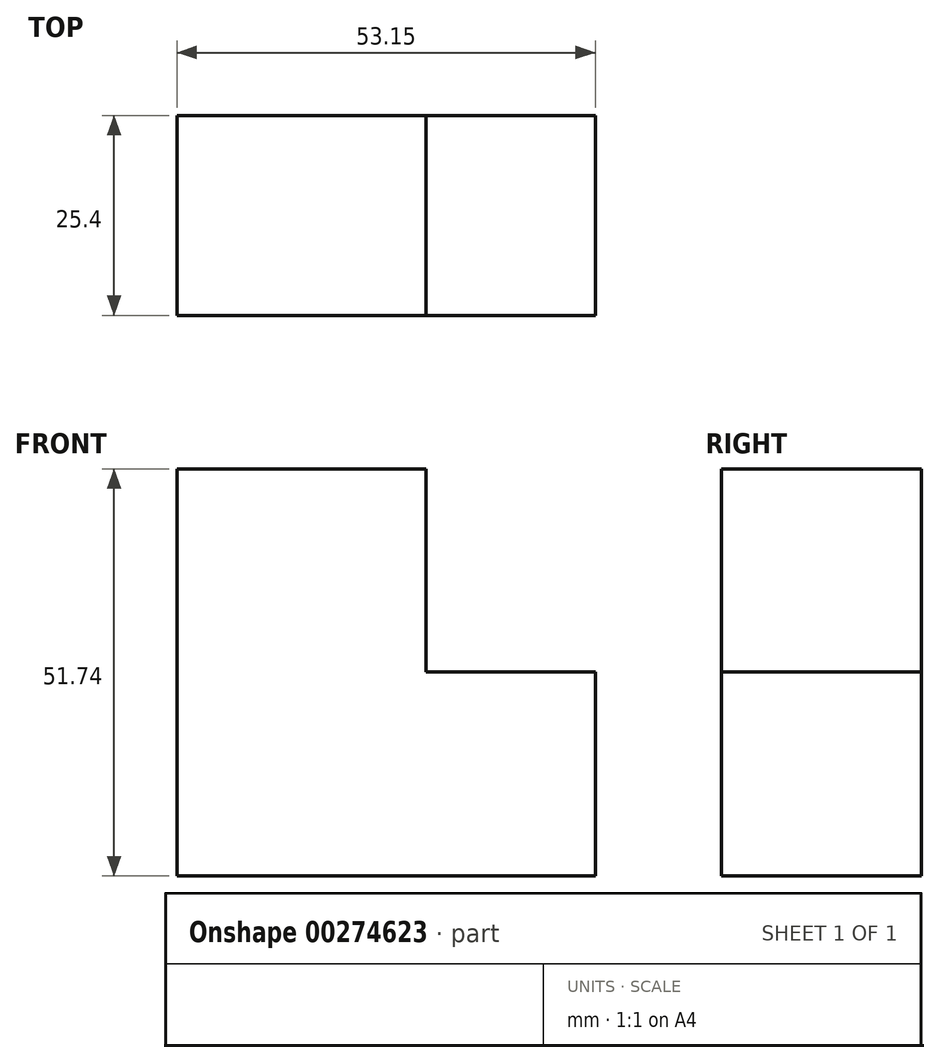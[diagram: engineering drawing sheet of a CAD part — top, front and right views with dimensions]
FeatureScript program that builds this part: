
annotation { "Feature Type Name" : "Feature", "Feature Type Description" : "" }
export const myFeature = defineFeature(function(context is Context, id is Id, definition is map)
    precondition{}
    {
        {
            var Q0;
            Q0=qCreatedBy(makeId("Front.planeOp"),FACE);
            var sketch = newSketch(context, id + "F0", { "sketchPlane" : qUnion([Q0])});
            skLineSegment(sketch, "E0", {"start": v(0, 0) * mm, "end": v(-53.15, 0) * mm});
            skLineSegment(sketch, "E1", {"start": v(-53.15, 0) * mm, "end": v(-53.15, 51.74) * mm});
            skLineSegment(sketch, "E2", {"start": v(-53.15, 51.74) * mm, "end": v(-21.49, 51.74) * mm});
            skLineSegment(sketch, "E3", {"start": v(-21.49, 51.74) * mm, "end": v(-21.49, 25.92) * mm});
            skLineSegment(sketch, "E4", {"start": v(-21.49, 25.92) * mm, "end": v(0, 25.92) * mm});
            skLineSegment(sketch, "E5", {"start": v(0, 25.92) * mm, "end": v(0, 0) * mm});
            skSolve(sketch);
        }
        {
            var Q0;
            Q0 = qSketchRegion(id + "F0", true);
            extrude(context, id + "F1", {"entities" : qUnion([Q0]), "depth" : 25.4 * mm});
        }
    });
